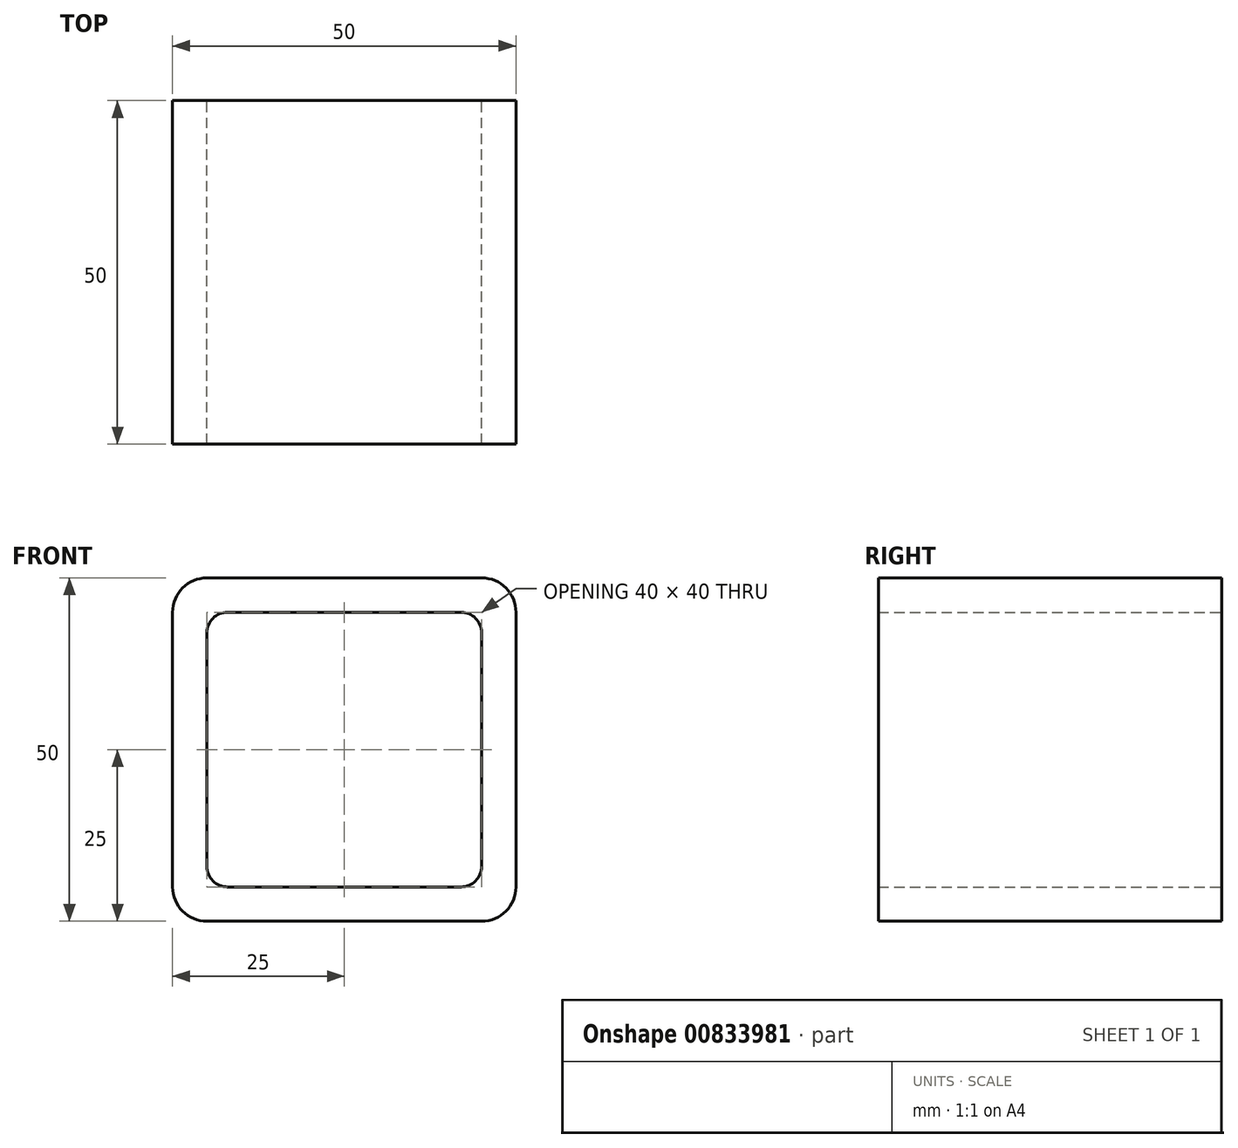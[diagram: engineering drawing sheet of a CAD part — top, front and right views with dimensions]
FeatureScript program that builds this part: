
annotation { "Feature Type Name" : "Feature", "Feature Type Description" : "" }
export const myFeature = defineFeature(function(context is Context, id is Id, definition is map)
    precondition{}
    {
        {
            var Q0;
            Q0=qCreatedBy(makeId("Front.planeOp"),FACE);
            var sketch = newSketch(context, id + "F0", { "sketchPlane" : qUnion([Q0])});
            skLineSegment(sketch, "E0.bottom", {"start": v(25, 25) * mm, "end": v(-25, 25) * mm});
            skLineSegment(sketch, "E0.top", {"start": v(25, -25) * mm, "end": v(-25, -25) * mm});
            skLineSegment(sketch, "E0.left", {"start": v(25, 25) * mm, "end": v(25, -25) * mm});
            skLineSegment(sketch, "E0.right", {"start": v(-25, 25) * mm, "end": v(-25, -25) * mm});
            skPoint(sketch, "E0.middle", {"position": v(0, 0) * mm});
            skLineSegment(sketch, "E1.bottom", {"start": v(20, 20) * mm, "end": v(-20, 20) * mm});
            skLineSegment(sketch, "E1.top", {"start": v(20, -20) * mm, "end": v(-20, -20) * mm});
            skLineSegment(sketch, "E1.left", {"start": v(20, 20) * mm, "end": v(20, -20) * mm});
            skLineSegment(sketch, "E1.right", {"start": v(-20, 20) * mm, "end": v(-20, -20) * mm});
            skSolve(sketch);
        }
        {
            var Q0;
            Q0=makeQuery(id+"F0.imprint","IMPRINT",FACE,{"disambiguationData":[TD([[makeQuery(id+"F0.imprint","IMPRINT",EDGE,{"derivedFrom":sQuery(id+"F0.wireOp",EDGE,"E0.bottom")}),1.0]])]});
            extrude(context, id + "F1", {"entities" : qUnion([Q0]), "depth" : 50 * mm, "offsetDistance" : 25 * mm});
        }
        {
            var Q0;
            Q0=makeQuery(id+"F1.opExtrude","SWEPT_EDGE",EDGE,{"disambiguationData":[OSD([sQuery(id+"F0.wireOp",EDGE,"E0.bottom"),sQuery(id+"F0.wireOp",EDGE,"E0.left")])]});
            var Q1;
            Q1=makeQuery(id+"F1.opExtrude","SWEPT_EDGE",EDGE,{"disambiguationData":[OSD([sQuery(id+"F0.wireOp",EDGE,"E0.bottom"),sQuery(id+"F0.wireOp",EDGE,"E0.right")])]});
            var Q2;
            Q2=makeQuery(id+"F1.opExtrude","SWEPT_EDGE",EDGE,{"disambiguationData":[OSD([sQuery(id+"F0.wireOp",EDGE,"E0.top"),sQuery(id+"F0.wireOp",EDGE,"E0.left")])]});
            var Q3;
            Q3=makeQuery(id+"F1.opExtrude","SWEPT_EDGE",EDGE,{"disambiguationData":[OSD([sQuery(id+"F0.wireOp",EDGE,"E0.top"),sQuery(id+"F0.wireOp",EDGE,"E0.right")])]});
            fillet(context, id + "F2", {"entities" : qUnion([Q0, Q1, Q2, Q3]), "radius" : 5 * mm, "tangentPropagation" : true, "allowEdgeOverflow" : false});
        }
        {
            var Q0;
            Q0=makeQuery(id+"F1.opExtrude","SWEPT_EDGE",EDGE,{"disambiguationData":[OSD([sQuery(id+"F0.wireOp",EDGE,"E1.bottom"),sQuery(id+"F0.wireOp",EDGE,"E1.left")])]});
            var Q1;
            Q1=makeQuery(id+"F1.opExtrude","SWEPT_EDGE",EDGE,{"disambiguationData":[OSD([sQuery(id+"F0.wireOp",EDGE,"E1.bottom"),sQuery(id+"F0.wireOp",EDGE,"E1.right")])]});
            var Q2;
            Q2=makeQuery(id+"F1.opExtrude","SWEPT_EDGE",EDGE,{"disambiguationData":[OSD([sQuery(id+"F0.wireOp",EDGE,"E1.top"),sQuery(id+"F0.wireOp",EDGE,"E1.right")])]});
            var Q3;
            Q3=makeQuery(id+"F1.opExtrude","SWEPT_EDGE",EDGE,{"disambiguationData":[OSD([sQuery(id+"F0.wireOp",EDGE,"E1.top"),sQuery(id+"F0.wireOp",EDGE,"E1.left")])]});
            fillet(context, id + "F3", {"entities" : qUnion([Q0, Q1, Q2, Q3]), "radius" : 3 * mm, "tangentPropagation" : true, "allowEdgeOverflow" : false});
        }
    });
